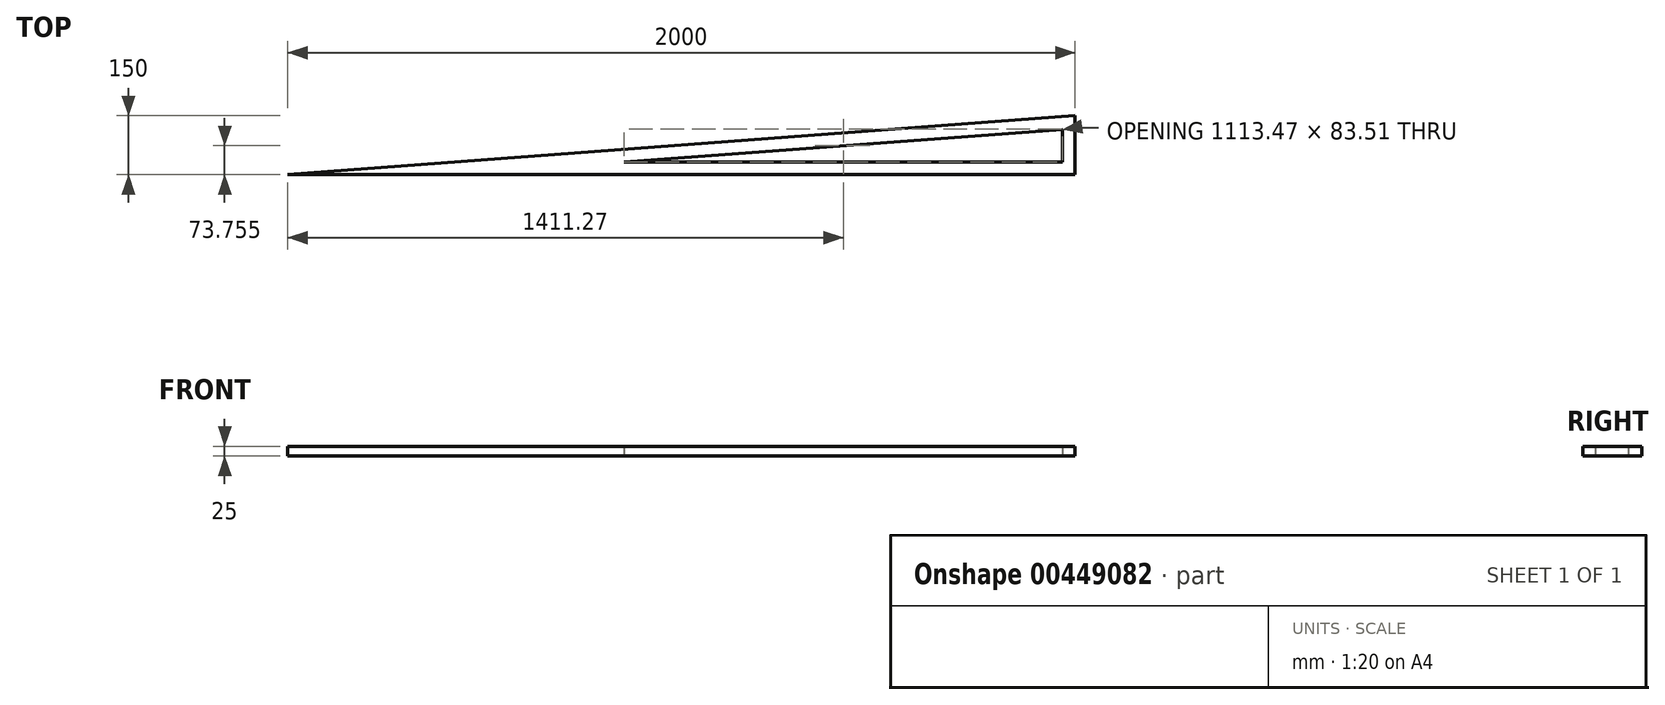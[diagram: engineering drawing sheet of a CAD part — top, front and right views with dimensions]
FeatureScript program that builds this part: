
annotation { "Feature Type Name" : "Feature", "Feature Type Description" : "" }
export const myFeature = defineFeature(function(context is Context, id is Id, definition is map)
    precondition{}
    {
        {
            var Q0;
            Q0=qCreatedBy(makeId("Top.planeOp"),FACE);
            var sketch = newSketch(context, id + "F0", { "sketchPlane" : qUnion([Q0])});
            skLineSegment(sketch, "E0", {"start": v(0, 0) * mm, "end": v(2000, 150) * mm});
            skLineSegment(sketch, "E1", {"start": v(2000, 150) * mm, "end": v(2000, 0) * mm});
            skLineSegment(sketch, "E2", {"start": v(2000, 0) * mm, "end": v(0, 0) * mm});
            skLineSegment(sketch, "E3.0", {"start": v(1968, 32) * mm, "end": v(854.53, 32) * mm});
            skLineSegment(sketch, "E3.1", {"start": v(1968, 115.51) * mm, "end": v(1968, 32) * mm});
            skLineSegment(sketch, "E3.2", {"start": v(854.53, 32) * mm, "end": v(1968, 115.51) * mm});
            skSolve(sketch);
        }
        {
            var Q0;
            Q0 = qSketchRegion(id + "F0", true);
            extrude(context, id + "F1", {"entities" : qUnion([Q0]), "depth" : 25 * mm});
        }
    });
